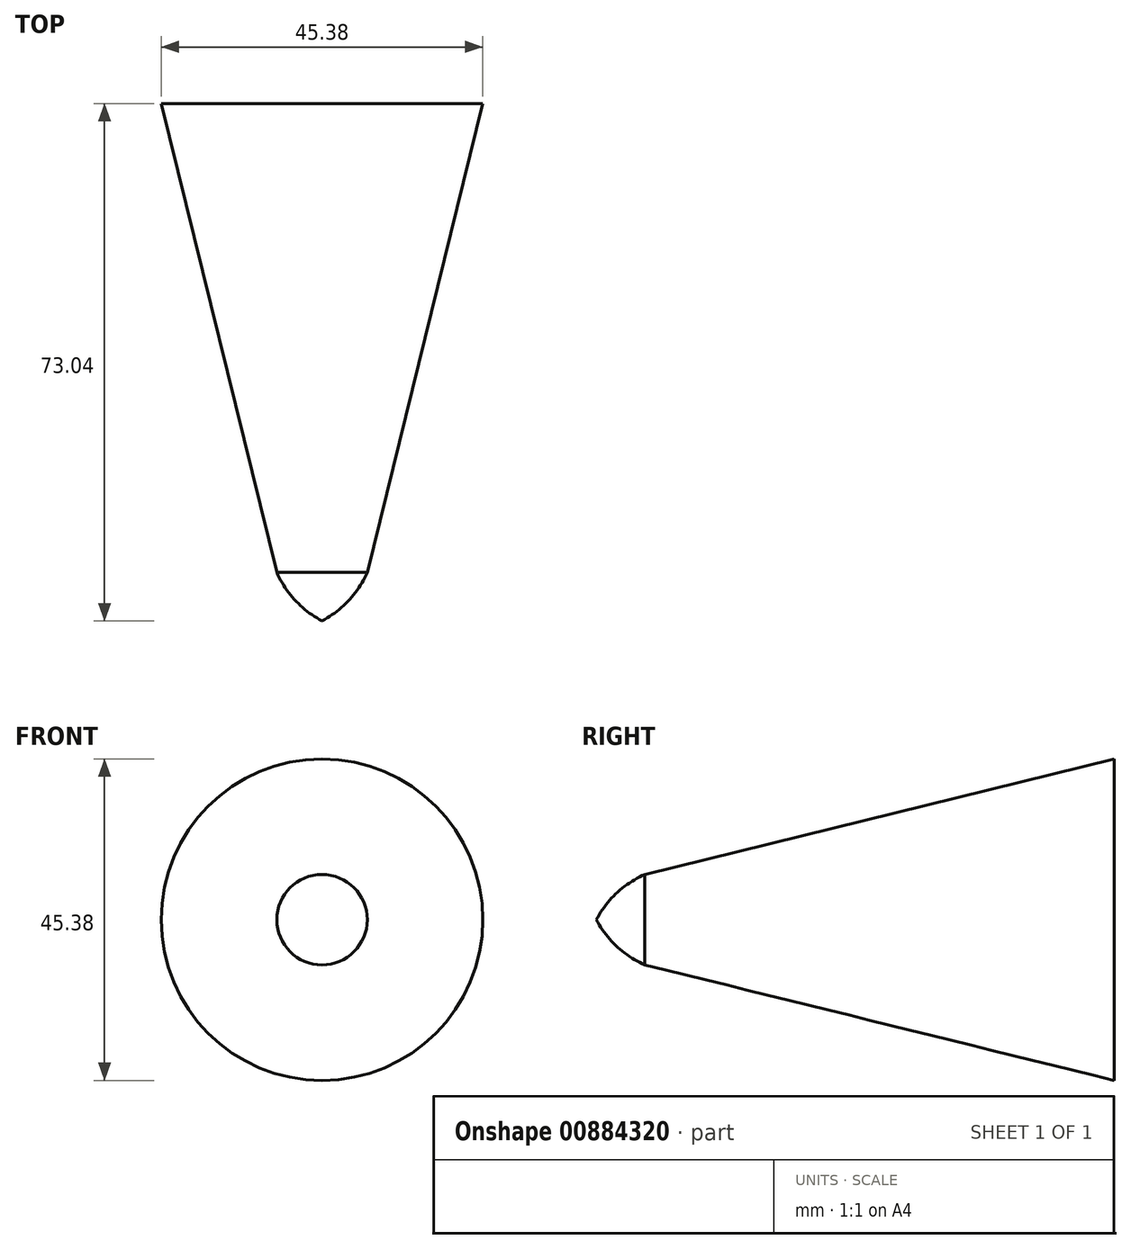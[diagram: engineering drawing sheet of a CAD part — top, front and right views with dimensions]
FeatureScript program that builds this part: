
annotation { "Feature Type Name" : "Feature", "Feature Type Description" : "" }
export const myFeature = defineFeature(function(context is Context, id is Id, definition is map)
    precondition{}
    {
        {
            var Q0;
            Q0=qCreatedBy(makeId("Right.planeOp"),FACE);
            var sketch = newSketch(context, id + "F0", { "sketchPlane" : qUnion([Q0])});
            skArc(sketch, "E0", {"start": v(6.85, 6.38) * mm, "mid": v(2.89, 3.77) * mm, "end": v(0, 0) * mm});
            skLineSegment(sketch, "E1", {"start": v(6.85, 6.38) * mm, "end": v(73.04, 22.7) * mm});
            skLineSegment(sketch, "E2", {"start": v(0, 0) * mm, "end": v(73.04, 0) * mm});
            skLineSegment(sketch, "E3", {"start": v(73.04, 0) * mm, "end": v(73.04, 22.7) * mm});
            skSolve(sketch);
        }
        {
            var Q0;
            Q0=makeQuery(id+"F0.imprint","IMPRINT",FACE,{"disambiguationData":[TD([[makeQuery(id+"F0.imprint","IMPRINT",EDGE,{"derivedFrom":sQuery(id+"F0.wireOp",EDGE,"E0")}),1.0]])]});
            var Q1;
            Q1=sQuery(id+"F0.wireOp",EDGE,"E2");
            revolve(context, id + "F1", {"surfaceOperationType" : NewSurfaceOperationType.NEW, "entities" : qUnion([Q0]), "axis" : qUnion([Q1]), "revolveType" : RevolveType.FULL});
        }
    });
